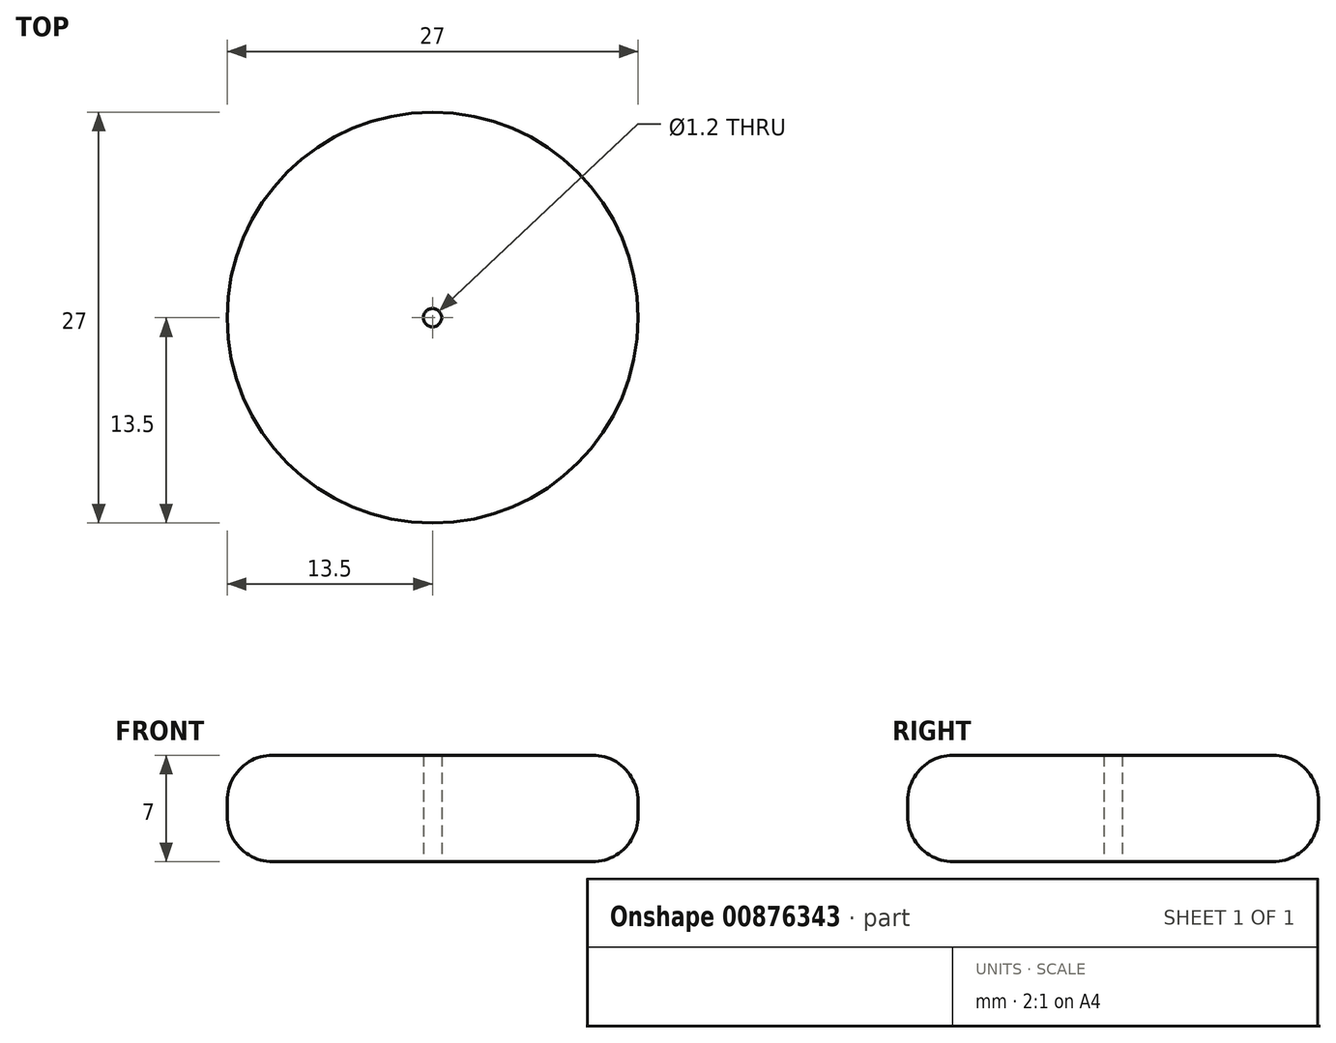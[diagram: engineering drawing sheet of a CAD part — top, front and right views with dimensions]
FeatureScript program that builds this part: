
annotation { "Feature Type Name" : "Feature", "Feature Type Description" : "" }
export const myFeature = defineFeature(function(context is Context, id is Id, definition is map)
    precondition{}
    {
        {
            var Q0;
            Q0=qCreatedBy(makeId("Top.planeOp"),FACE);
            var sketch = newSketch(context, id + "F0", { "sketchPlane" : qUnion([Q0])});
            skCircle(sketch, "E0", {"center": v(0, 0) * mm, "radius": 13.5 * mm});
            skSolve(sketch);
        }
        {
            var Q0;
            Q0=qSketchRegion(id+"F0",true);
            extrude(context, id + "F1", {"entities" : qUnion([Q0]), "depth" : 7 * mm, "offsetDistance" : 25 * mm});
        }
        {
            var Q0;
            Q0=sQuery(id+"F0.wireOp",VERTEX,"E0.center");
            var Q1;
            Q1=makeQuery(id+"F1.opExtrude","SWEPT_BODY",BODY,{"disambiguationData":[OSD([sQuery(id+"F0.wireOp",EDGE,"E0")])]});
            hole(context, id + "F2", {"style" : HoleStyle.SIMPLE, "endStyle" : HoleEndStyle.THROUGH, "oppositeDirection" : true, "holeDiameter" : 1.2 * mm, "majorDiameter" : 5 * mm, "isTappedThrough" : true, "tappedDepth" : 12 * mm, "tapClearance" : 3, "locations" : qUnion([Q0]), "scope" : qUnion([Q1])});
        }
        {
            var Q0;
            Q0=makeQuery(id+"F1.opExtrude","CAP_EDGE",EDGE,{"disambiguationData":[OSD([sQuery(id+"F0.wireOp",EDGE,"E0")])],"isStart":true});
            var Q1;
            Q1=makeQuery(id+"F1.opExtrude","CAP_EDGE",EDGE,{"disambiguationData":[OSD([sQuery(id+"F0.wireOp",EDGE,"E0")])],"isStart":false});
            fillet(context, id + "F3", {"entities" : qUnion([Q0, Q1]), "radius" : 3 * mm, "tangentPropagation" : true, "allowEdgeOverflow" : false});
        }
    });
